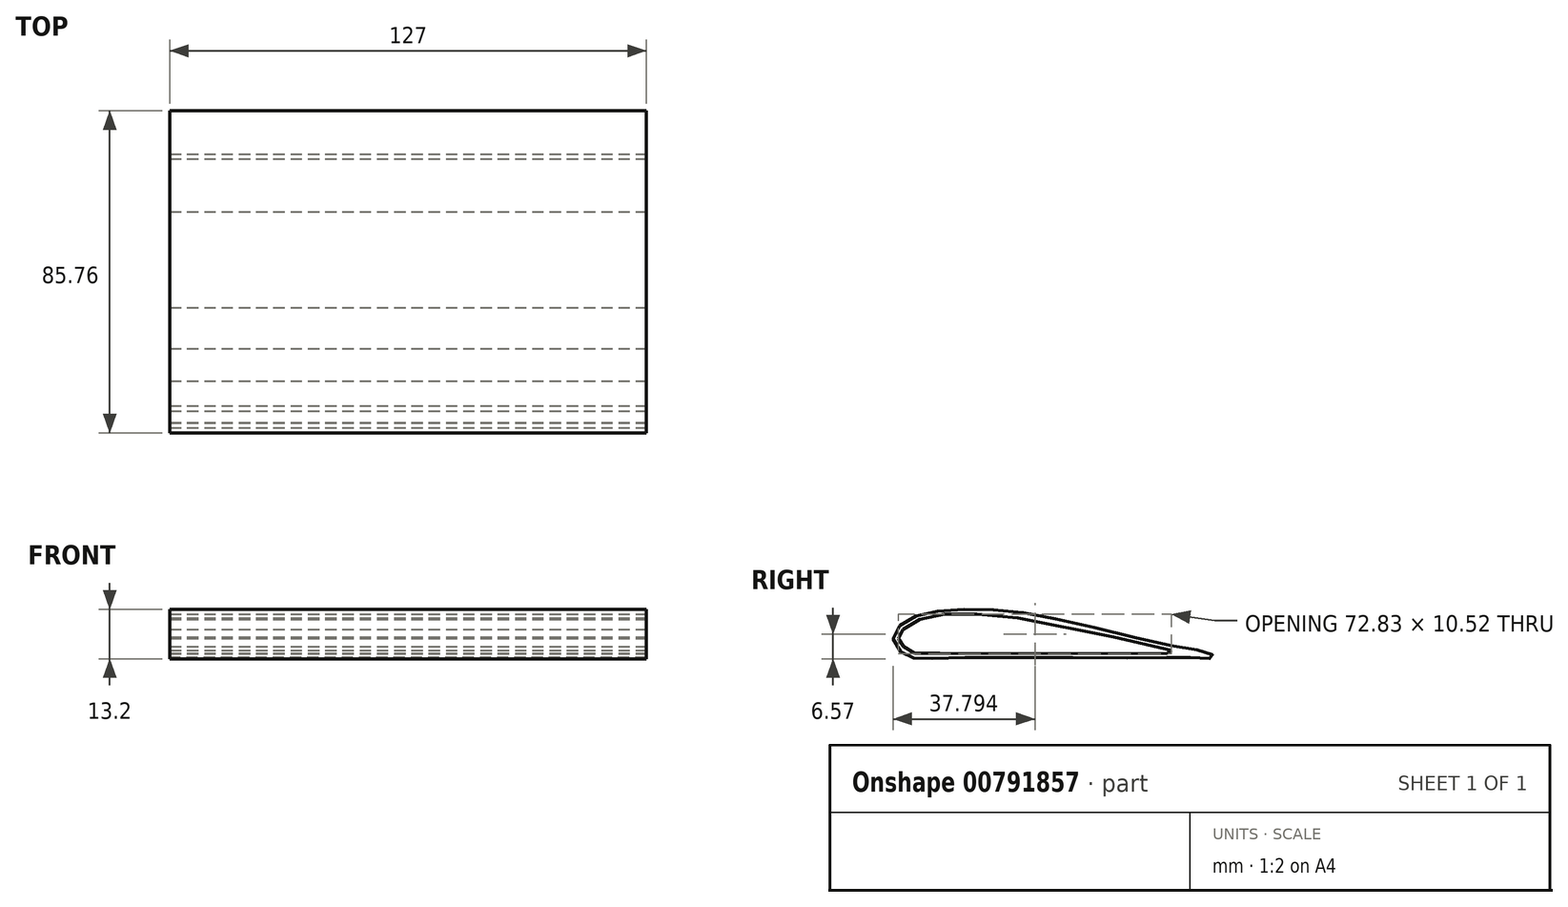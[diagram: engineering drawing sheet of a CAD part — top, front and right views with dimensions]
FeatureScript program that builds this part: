
annotation { "Feature Type Name" : "Feature", "Feature Type Description" : "" }
export const myFeature = defineFeature(function(context is Context, id is Id, definition is map)
    precondition{}
    {
        {
            var Q0;
            Q0=qCreatedBy(makeId("Right.planeOp"),FACE);
            var sketch = newSketch(context, id + "F0", { "sketchPlane" : qUnion([Q0])});
            skFitSpline(sketch, "E0", {"points": [v(-11.32, 0) * mm, v(-14.91, 1.78) * mm, v(-16.78, 5.52) * mm, v(-13.62, 9.68) * mm, v(-6, 12.27) * mm, v(9.07, 12.84) * mm, v(29.32, 9.82) * mm, v(58.9, 2.93) * mm, v(67.66, 1.2) * mm, v(68.95, 0) * mm, v(64.93, 0) * mm, v(52.58, 0) * mm, v(0, 0) * mm, v(-11.32, 0) * mm]});
            skSolve(sketch);
        }
        {
            var Q0;
            Q0 = qSketchRegion(id + "F0", true);
            extrude(context, id + "F1", {"entities" : qUnion([Q0]), "depth" : 63.5 * mm, "offsetDistance" : 25.4 * mm, "hasSecondDirection" : true, "secondDirectionOppositeDirection" : true, "secondDirectionDepth" : 63.5 * mm});
        }
        {
            var Q0;
            Q0=makeQuery(id+"F1.opExtrude","CAP_FACE",FACE,{"disambiguationData":[OSD([sQuery(id+"F0.wireOp",EDGE,"E0")])],"isStart":false});
            var sketch = newSketch(context, id + "F2", { "sketchPlane" : qUnion([Q0])});
            skLineSegment(sketch, "E1", {"start": v(-4.4, 1.17) * mm, "end": v(-11.05, 1.17) * mm});
            skLineSegment(sketch, "E2", {"start": v(-11.05, 1.17) * mm, "end": v(-14.02, 3.06) * mm});
            skLineSegment(sketch, "E3", {"start": v(-14.02, 3.06) * mm, "end": v(-15.41, 5.14) * mm});
            skLineSegment(sketch, "E4", {"start": v(-15.41, 5.14) * mm, "end": v(-14.12, 7.52) * mm});
            skLineSegment(sketch, "E5", {"start": v(-14.12, 7.52) * mm, "end": v(-9.66, 10.2) * mm});
            skLineSegment(sketch, "E6", {"start": v(-9.66, 10.2) * mm, "end": v(-3, 11.59) * mm});
            skLineSegment(sketch, "E7", {"start": v(-3, 11.59) * mm, "end": v(5.62, 11.59) * mm});
            skLineSegment(sketch, "E8", {"start": v(5.62, 11.59) * mm, "end": v(16.54, 10.6) * mm});
            skLineSegment(sketch, "E9", {"start": v(16.54, 10.6) * mm, "end": v(42.04, 5.54) * mm});
            skLineSegment(sketch, "E10", {"start": v(42.04, 5.54) * mm, "end": v(57.42, 1.96) * mm});
            skLineSegment(sketch, "E11", {"start": v(57.42, 1.96) * mm, "end": v(56.13, 1.07) * mm});
            skLineSegment(sketch, "E12", {"start": v(56.13, 1.07) * mm, "end": v(-4.4, 1.17) * mm});
            skSolve(sketch);
        }
        {
            var Q0;
            Q0 = qSketchRegion(id + "F2", true);
            extrude(context, id + "F3", {"entities" : qUnion([Q0]), "operationType" : NewBodyOperationType.REMOVE, "oppositeDirection" : true, "depth" : 127 * mm, "offsetDistance" : 25.4 * mm});
        }
    });
